annotation { "Feature Type Name" : "Feature", "Feature Type Description" : "" }
export const myFeature = defineFeature(function(context is Context, id is Id, definition is map)
    precondition{}
    {
        {
            var Q0;
            Q0=qCreatedBy(makeId("Front.planeOp"),FACE);
            var sketch = newSketch(context, id + "F0", { "sketchPlane" : qUnion([Q0])});
            skLineSegment(sketch, "E0.bottom", {"start": v(-44.68, 30.46) * mm, "end": v(44.68, 30.46) * mm});
            skLineSegment(sketch, "E0.top", {"start": v(-44.68, -30.46) * mm, "end": v(44.68, -30.46) * mm});
            skLineSegment(sketch, "E0.left", {"start": v(-44.68, 30.46) * mm, "end": v(-44.68, -30.46) * mm});
            skLineSegment(sketch, "E0.right", {"start": v(44.68, 30.46) * mm, "end": v(44.68, -30.46) * mm});
            skPoint(sketch, "E0.middle", {"position": v(0, 0) * mm});
            skSolve(sketch);
        }
        {
            var Q0;
            Q0=makeQuery(id+"F0.imprint","IMPRINT",FACE,{"disambiguationData":[TD([[makeQuery(id+"F0.imprint","IMPRINT",EDGE,{"derivedFrom":sQuery(id+"F0.wireOp",EDGE,"E0.bottom")}),-1.0]])]});
            extrude(context, id + "F1", {"entities" : qUnion([Q0]), "endBound" : BoundingType.SYMMETRIC, "depth" : 99.2 * mm});
        }
        {
            var Q0;
            Q0=makeQuery(id+"F1.opExtrude","SWEPT_FACE",FACE,{"disambiguationData":[OSD([sQuery(id+"F0.wireOp",EDGE,"E0.bottom")])]});
            shell(context, id + "F2", {"entities" : qUnion([Q0]), "thickness" : 2.5 * mm});
        }
        {
            var Q0;
            Q0=makeQuery(id+"F1.opExtrude","CAP_FACE",FACE,{"disambiguationData":[OSD([sQuery(id+"F0.wireOp",EDGE,"E0.bottom"),sQuery(id+"F0.wireOp",EDGE,"E0.top"),sQuery(id+"F0.wireOp",EDGE,"E0.left"),sQuery(id+"F0.wireOp",EDGE,"E0.right")])],"isStart":false});
            var sketch = newSketch(context, id + "F3", { "sketchPlane" : qUnion([Q0])});
            skLineSegment(sketch, "E1.bottom", {"start": v(-44.68, 30.46) * mm, "end": v(-36.59, 30.46) * mm});
            skLineSegment(sketch, "E1.top", {"start": v(-44.68, -30.46) * mm, "end": v(-36.59, -30.46) * mm});
            skLineSegment(sketch, "E1.left", {"start": v(-44.68, 30.46) * mm, "end": v(-44.68, -30.46) * mm});
            skLineSegment(sketch, "E1.right", {"start": v(-36.59, 30.46) * mm, "end": v(-36.59, -30.46) * mm});
            skLineSegment(sketch, "E2.bottom", {"start": v(44.68, 30.46) * mm, "end": v(36.58, 30.46) * mm});
            skLineSegment(sketch, "E2.top", {"start": v(44.68, -30.46) * mm, "end": v(36.58, -30.46) * mm});
            skLineSegment(sketch, "E2.left", {"start": v(44.68, 30.46) * mm, "end": v(44.68, -30.46) * mm});
            skLineSegment(sketch, "E2.right", {"start": v(36.58, 30.46) * mm, "end": v(36.58, -30.46) * mm});
            skSolve(sketch);
        }
        {
            var Q0;
            Q0=makeQuery(id+"F3.imprint","IMPRINT",FACE,{"disambiguationData":[TD([[makeQuery(id+"F3.imprint","IMPRINT",EDGE,{"derivedFrom":sQuery(id+"F3.wireOp",EDGE,"E1.bottom")}),-1.0]])]});
            var Q1;
            Q1=makeQuery(id+"F3.imprint","IMPRINT",FACE,{"disambiguationData":[TD([[makeQuery(id+"F3.imprint","IMPRINT",EDGE,{"derivedFrom":sQuery(id+"F3.wireOp",EDGE,"E2.bottom")}),-1.0]])]});
            extrude(context, id + "F4", {"entities" : qUnion([Q0, Q1]), "operationType" : NewBodyOperationType.ADD, "depth" : 2.8 * mm});
        }
        {
            var Q0;
            Q0=makeQuery(id+"F4.opExtrude","CAP_FACE",FACE,{"disambiguationData":[OSD([sQuery(id+"F3.wireOp",EDGE,"E1.bottom"),sQuery(id+"F3.wireOp",EDGE,"E1.top"),sQuery(id+"F3.wireOp",EDGE,"E1.left"),sQuery(id+"F3.wireOp",EDGE,"E1.right")])],"isStart":false});
            var Q1;
            Q1=makeQuery(id+"F4.opExtrude","CAP_FACE",FACE,{"disambiguationData":[OSD([sQuery(id+"F3.wireOp",EDGE,"E2.bottom"),sQuery(id+"F3.wireOp",EDGE,"E2.top"),sQuery(id+"F3.wireOp",EDGE,"E2.left"),sQuery(id+"F3.wireOp",EDGE,"E2.right")])],"isStart":false});
            var Q2;
            Q2=makeQuery(id+"F1.opExtrude","CAP_FACE",FACE,{"disambiguationData":[OSD([sQuery(id+"F0.wireOp",EDGE,"E0.bottom"),sQuery(id+"F0.wireOp",EDGE,"E0.top"),sQuery(id+"F0.wireOp",EDGE,"E0.left"),sQuery(id+"F0.wireOp",EDGE,"E0.right")])],"isStart":true});
            shell(context, id + "F5", {"entities" : qUnion([Q0, Q1, Q2]), "thickness" : 2.5 * mm});
        }
        {
            var Q0;
            Q0=makeQuery(id+"F4.boolean.opBoolean","MERGE",FACE,{"derivedFrom":[makeQuery(id+"F1.opExtrude","SWEPT_FACE",FACE,{"disambiguationData":[OSD([sQuery(id+"F0.wireOp",EDGE,"E0.right")])]}),makeQuery(id+"F4.opExtrude","SWEPT_FACE",FACE,{"disambiguationData":[OSD([sQuery(id+"F3.wireOp",EDGE,"E2.left")])]})]});
            var sketch = newSketch(context, id + "F6", { "sketchPlane" : qUnion([Q0])});
            skLineSegment(sketch, "E3.bottom", {"start": v(-52.4, 30.46) * mm, "end": v(-44.7, 30.46) * mm});
            skLineSegment(sketch, "E3.top", {"start": v(-52.4, -30.46) * mm, "end": v(-44.7, -30.46) * mm});
            skLineSegment(sketch, "E3.left", {"start": v(-52.4, 30.46) * mm, "end": v(-52.4, -30.46) * mm});
            skLineSegment(sketch, "E3.right", {"start": v(-44.7, 30.46) * mm, "end": v(-44.7, -30.46) * mm});
            skSolve(sketch);
        }
        {
            var Q0;
            Q0=makeQuery(id+"F6.imprint","IMPRINT",FACE,{"disambiguationData":[TD([[makeQuery(id+"F6.imprint","IMPRINT",EDGE,{"derivedFrom":sQuery(id+"F6.wireOp",EDGE,"E3.bottom")}),-1.0]])]});
            extrude(context, id + "F7", {"entities" : qUnion([Q0]), "operationType" : NewBodyOperationType.ADD, "depth" : 1 * mm});
        }
        {
            var Q0;
            Q0=makeQuery(id+"F7.opExtrude","CAP_FACE",FACE,{"disambiguationData":[OSD([sQuery(id+"F6.wireOp",EDGE,"E3.bottom"),sQuery(id+"F6.wireOp",EDGE,"E3.top"),sQuery(id+"F6.wireOp",EDGE,"E3.left"),sQuery(id+"F6.wireOp",EDGE,"E3.right")])],"isStart":false});
            var Q1;
            Q1=makeQuery(id+"F5.opShell","OFFSET_FACE",FACE,{"disambiguationData":[OSD([sQuery(id+"F0.wireOp",EDGE,"E0.left"),sQuery(id+"F3.wireOp",EDGE,"E1.left")])]});
            shell(context, id + "F8", {"entities" : qUnion([Q0, Q1]), "thickness" : 2.5 * mm});
        }
        {
            var Q0;
            Q0=makeQuery(id+"F4.boolean.opBoolean","MERGE",FACE,{"derivedFrom":[makeQuery(id+"F1.opExtrude","SWEPT_FACE",FACE,{"disambiguationData":[OSD([sQuery(id+"F0.wireOp",EDGE,"E0.left")])]}),makeQuery(id+"F4.opExtrude","SWEPT_FACE",FACE,{"disambiguationData":[OSD([sQuery(id+"F3.wireOp",EDGE,"E1.left")])]})]});
            var sketch = newSketch(context, id + "F9", { "sketchPlane" : qUnion([Q0])});
            skLineSegment(sketch, "E4.bottom", {"start": v(-49.6, 30.46) * mm, "end": v(-40.98, 30.46) * mm});
            skLineSegment(sketch, "E4.top", {"start": v(-49.6, -30.46) * mm, "end": v(-40.98, -30.46) * mm});
            skLineSegment(sketch, "E4.left", {"start": v(-49.6, 30.46) * mm, "end": v(-49.6, -30.46) * mm});
            skLineSegment(sketch, "E4.right", {"start": v(-40.98, 30.46) * mm, "end": v(-40.98, -30.46) * mm});
            skLineSegment(sketch, "E5.bottom", {"start": v(52.4, 30.46) * mm, "end": v(44.29, 30.46) * mm});
            skLineSegment(sketch, "E5.top", {"start": v(52.4, -30.46) * mm, "end": v(44.29, -30.46) * mm});
            skLineSegment(sketch, "E5.left", {"start": v(52.4, 30.46) * mm, "end": v(52.4, -30.46) * mm});
            skLineSegment(sketch, "E5.right", {"start": v(44.29, 30.46) * mm, "end": v(44.29, -30.46) * mm});
            skSolve(sketch);
        }
        {
            var Q0;
            Q0=makeQuery(id+"F9.imprint","IMPRINT",FACE,{"disambiguationData":[TD([[makeQuery(id+"F9.imprint","IMPRINT",EDGE,{"derivedFrom":sQuery(id+"F9.wireOp",EDGE,"E4.bottom")}),1.0]])]});
            var Q1;
            Q1=makeQuery(id+"F9.imprint","IMPRINT",FACE,{"disambiguationData":[TD([[makeQuery(id+"F9.imprint","IMPRINT",EDGE,{"derivedFrom":sQuery(id+"F9.wireOp",EDGE,"E5.bottom")}),1.0]])]});
            extrude(context, id + "F10", {"entities" : qUnion([Q0, Q1]), "operationType" : NewBodyOperationType.ADD, "depth" : 1.9 * mm});
        }
        {
            var Q0;
            Q0=makeQuery(id+"F10.opExtrude","CAP_FACE",FACE,{"disambiguationData":[OSD([sQuery(id+"F9.wireOp",EDGE,"E4.bottom"),sQuery(id+"F9.wireOp",EDGE,"E4.top"),sQuery(id+"F9.wireOp",EDGE,"E4.left"),sQuery(id+"F9.wireOp",EDGE,"E4.right")])],"isStart":false});
            var Q1;
            Q1=makeQuery(id+"F10.opExtrude","CAP_FACE",FACE,{"disambiguationData":[OSD([sQuery(id+"F9.wireOp",EDGE,"E5.bottom"),sQuery(id+"F9.wireOp",EDGE,"E5.top"),sQuery(id+"F9.wireOp",EDGE,"E5.left"),sQuery(id+"F9.wireOp",EDGE,"E5.right")])],"isStart":false});
            shell(context, id + "F11", {"entities" : qUnion([Q0, Q1]), "thickness" : 2.5 * mm});
        }
        {
            var Q0;
            Q0=makeQuery(id+"F10.boolean.opBoolean","MERGE",FACE,{"derivedFrom":[makeQuery(id+"F1.opExtrude","CAP_FACE",FACE,{"disambiguationData":[OSD([sQuery(id+"F0.wireOp",EDGE,"E0.bottom"),sQuery(id+"F0.wireOp",EDGE,"E0.top"),sQuery(id+"F0.wireOp",EDGE,"E0.left"),sQuery(id+"F0.wireOp",EDGE,"E0.right")])],"isStart":true}),makeQuery(id+"F10.opExtrude","SWEPT_FACE",FACE,{"disambiguationData":[OSD([sQuery(id+"F9.wireOp",EDGE,"E4.left")])]})]});
            var sketch = newSketch(context, id + "F12", { "sketchPlane" : qUnion([Q0])});
            skSolve(sketch);
        }
        {
            var Q0;
            Q0=makeQuery(id+"F4.boolean.opBoolean","MERGE",FACE,{"derivedFrom":[makeQuery(id+"F1.opExtrude","SWEPT_FACE",FACE,{"disambiguationData":[OSD([sQuery(id+"F0.wireOp",EDGE,"E0.right")])]}),makeQuery(id+"F4.opExtrude","SWEPT_FACE",FACE,{"disambiguationData":[OSD([sQuery(id+"F3.wireOp",EDGE,"E2.left")])]})]});
            var sketch = newSketch(context, id + "F13", { "sketchPlane" : qUnion([Q0])});
            skLineSegment(sketch, "E6.bottom", {"start": v(49.6, 30.46) * mm, "end": v(39.53, 30.46) * mm});
            skLineSegment(sketch, "E6.top", {"start": v(49.6, -30.46) * mm, "end": v(39.53, -30.46) * mm});
            skLineSegment(sketch, "E6.left", {"start": v(49.6, 30.46) * mm, "end": v(49.6, -30.46) * mm});
            skLineSegment(sketch, "E6.right", {"start": v(39.53, 30.46) * mm, "end": v(39.53, -30.46) * mm});
            skSolve(sketch);
        }
        {
            var Q0;
            Q0=makeQuery(id+"F13.imprint","IMPRINT",FACE,{"disambiguationData":[TD([[makeQuery(id+"F13.imprint","IMPRINT",EDGE,{"derivedFrom":sQuery(id+"F13.wireOp",EDGE,"E6.bottom")}),-1.0]])]});
            extrude(context, id + "F14", {"entities" : qUnion([Q0]), "operationType" : NewBodyOperationType.ADD, "depth" : 2.5 * mm});
        }
        {
            var Q0;
            Q0=makeQuery(id+"F14.opExtrude","CAP_FACE",FACE,{"disambiguationData":[OSD([sQuery(id+"F13.wireOp",EDGE,"E6.bottom"),sQuery(id+"F13.wireOp",EDGE,"E6.top"),sQuery(id+"F13.wireOp",EDGE,"E6.left"),sQuery(id+"F13.wireOp",EDGE,"E6.right")])],"isStart":false});
            shell(context, id + "F15", {"entities" : qUnion([Q0]), "thickness" : 2.5 * mm});
        }
        {
            var Q0;
            Q0=makeQuery(id+"F14.boolean.opBoolean","MERGE",FACE,{"derivedFrom":[makeQuery(id+"F10.boolean.opBoolean","MERGE",FACE,{"derivedFrom":[makeQuery(id+"F1.opExtrude","CAP_FACE",FACE,{"disambiguationData":[OSD([sQuery(id+"F0.wireOp",EDGE,"E0.bottom"),sQuery(id+"F0.wireOp",EDGE,"E0.top"),sQuery(id+"F0.wireOp",EDGE,"E0.left"),sQuery(id+"F0.wireOp",EDGE,"E0.right")])],"isStart":true}),makeQuery(id+"F10.opExtrude","SWEPT_FACE",FACE,{"disambiguationData":[OSD([sQuery(id+"F9.wireOp",EDGE,"E4.left")])]})]}),makeQuery(id+"F14.opExtrude","SWEPT_FACE",FACE,{"disambiguationData":[OSD([sQuery(id+"F13.wireOp",EDGE,"E6.left")])]})]});
            var sketch = newSketch(context, id + "F16", { "sketchPlane" : qUnion([Q0])});
            skLineSegment(sketch, "E7.bottom", {"start": v(-47.18, 30.46) * mm, "end": v(-37.77, 30.46) * mm});
            skLineSegment(sketch, "E7.top", {"start": v(-47.18, -30.46) * mm, "end": v(-37.77, -30.46) * mm});
            skLineSegment(sketch, "E7.left", {"start": v(-47.18, 30.46) * mm, "end": v(-47.18, -30.46) * mm});
            skLineSegment(sketch, "E7.right", {"start": v(-37.77, 30.46) * mm, "end": v(-37.77, -30.46) * mm});
            skLineSegment(sketch, "E8.bottom", {"start": v(46.58, 30.46) * mm, "end": v(36.94, 30.46) * mm});
            skLineSegment(sketch, "E8.top", {"start": v(46.58, -30.46) * mm, "end": v(36.94, -30.46) * mm});
            skLineSegment(sketch, "E8.left", {"start": v(46.58, 30.46) * mm, "end": v(46.58, -30.46) * mm});
            skLineSegment(sketch, "E8.right", {"start": v(36.94, 30.46) * mm, "end": v(36.94, -30.46) * mm});
            skSolve(sketch);
        }
        {
            var Q0;
            Q0 = qSketchRegion(id + "F16", true);
            extrude(context, id + "F17", {"entities" : qUnion([Q0]), "operationType" : NewBodyOperationType.ADD, "depth" : 1.4 * mm});
        }
        {
            var Q0;
            Q0=makeQuery(id+"F17.opExtrude","CAP_FACE",FACE,{"disambiguationData":[OSD([sQuery(id+"F16.wireOp",EDGE,"E7.bottom"),sQuery(id+"F16.wireOp",EDGE,"E7.top"),sQuery(id+"F16.wireOp",EDGE,"E7.left"),sQuery(id+"F16.wireOp",EDGE,"E7.right")])],"isStart":false});
            var Q1;
            Q1=makeQuery(id+"F17.opExtrude","CAP_FACE",FACE,{"disambiguationData":[OSD([sQuery(id+"F16.wireOp",EDGE,"E8.bottom"),sQuery(id+"F16.wireOp",EDGE,"E8.top"),sQuery(id+"F16.wireOp",EDGE,"E8.left"),sQuery(id+"F16.wireOp",EDGE,"E8.right")])],"isStart":false});
            shell(context, id + "F18", {"entities" : qUnion([Q0, Q1]), "thickness" : 2.5 * mm});
        }
        {
            var Q0;
            Q0=makeQuery(id+"F10.opExtrude","CAP_EDGE",EDGE,{"disambiguationData":[OSD([sQuery(id+"F9.wireOp",EDGE,"E5.left")])],"isStart":false});
            var Q1;
            Q1=makeQuery(id+"F7.opExtrude","CAP_EDGE",EDGE,{"disambiguationData":[OSD([sQuery(id+"F6.wireOp",EDGE,"E3.left")])],"isStart":false});
            var Q2;
            Q2=makeQuery(id+"F17.opExtrude","CAP_EDGE",EDGE,{"disambiguationData":[OSD([sQuery(id+"F16.wireOp",EDGE,"E7.left")])],"isStart":false});
            var Q3;
            Q3=makeQuery(id+"F17.opExtrude","CAP_EDGE",EDGE,{"disambiguationData":[OSD([sQuery(id+"F16.wireOp",EDGE,"E8.left")])],"isStart":false});
            fillet(context, id + "F19", {"entities" : qUnion([Q0, Q1, Q2, Q3]), "radius" : 5 * mm, "tangentPropagation" : true, "allowEdgeOverflow" : false});
        }
        {
            var Q0;
            Q0=makeQuery(id+"F12.imprint","IMPRINT",FACE,{"disambiguationData":[TD([[makeQuery(id+"F12.imprint","IMPRINT",EDGE,{"derivedFrom":makeQuery(id+"F1.opExtrude","CAP_EDGE",EDGE,{"disambiguationData":[OSD([sQuery(id+"F0.wireOp",EDGE,"E0.right")])],"isStart":true})}),1.0]])]});
            var sketch = newSketch(context, id + "F20", { "sketchPlane" : qUnion([Q0])});
            skText(sketch, "E9", { "text": "Yellow Jacket\n     Football", "fontName": "DroidSansMono.ttf"});
            const initialGuessF20  = {"E9": [-0.03725, 0, 1, 0, 0.00528]};
            skSetInitialGuess(sketch, initialGuessF20);
            skSolve(sketch);
        }
        {
            var Q0;
            Q0 = qConstructionFilter(qBodyType(qCreatedBy(id + "F20" ,EDGE), BodyType.WIRE), ConstructionObject.NO);
            extrude(context, id + "F21", {"bodyType" : ToolBodyType.SURFACE, "surfaceEntities" : qUnion([Q0]), "depth" : 1.6 * mm});
        }
        {
            var Q0;
            Q0=makeQuery(id+"F1.opExtrude","CAP_FACE",FACE,{"disambiguationData":[OSD([sQuery(id+"F0.wireOp",EDGE,"E0.bottom"),sQuery(id+"F0.wireOp",EDGE,"E0.top"),sQuery(id+"F0.wireOp",EDGE,"E0.left"),sQuery(id+"F0.wireOp",EDGE,"E0.right")])],"isStart":false});
            var sketch = newSketch(context, id + "F22", { "sketchPlane" : qUnion([Q0])});
            skText(sketch, "E10", { "text": "Yellow Jacket \n  Football", "fontName": "DroidSansMono.ttf"});
            skPoint(sketch, "E10.secondSnap0", {"position": v(-36.59, 0) * mm});
            const initialGuessF22  = {"E10": [-0.03158, 0, 1, 0, 0.0052]};
            skSetInitialGuess(sketch, initialGuessF22);
            skSolve(sketch);
        }
        {
            var Q0;
            Q0 = qSketchRegion(id + "F22", true);
            extrude(context, id + "F23", {"entities" : qUnion([Q0]), "operationType" : NewBodyOperationType.ADD, "depth" : 0.6 * mm});
        }
        {
            var Q0;
            Q0=makeQuery(id+"F4.boolean.opBoolean","MERGE",FACE,{"derivedFrom":[makeQuery(id+"F1.opExtrude","SWEPT_FACE",FACE,{"disambiguationData":[OSD([sQuery(id+"F0.wireOp",EDGE,"E0.right")])]}),makeQuery(id+"F4.opExtrude","SWEPT_FACE",FACE,{"disambiguationData":[OSD([sQuery(id+"F3.wireOp",EDGE,"E2.left")])]})]});
            var sketch = newSketch(context, id + "F24", { "sketchPlane" : qUnion([Q0])});
            skText(sketch, "E11", { "text": "STATE CHAMPS", "fontName": "DroidSansMono.ttf"});
            skPoint(sketch, "E11.firstSnap0", {"position": v(-44.7, 0) * mm});
            const initialGuessF24  = {"E11": [-0.0443, 0, 1, 0, 0.0082]};
            skSetInitialGuess(sketch, initialGuessF24);
            skSolve(sketch);
        }
        {
            var Q0;
            Q0 = qSketchRegion(id + "F24", true);
            extrude(context, id + "F25", {"entities" : qUnion([Q0]), "operationType" : NewBodyOperationType.ADD, "depth" : 1 * mm});
        }
        {
            var Q0;
            Q0=makeQuery(id+"F4.boolean.opBoolean","MERGE",FACE,{"derivedFrom":[makeQuery(id+"F1.opExtrude","SWEPT_FACE",FACE,{"disambiguationData":[OSD([sQuery(id+"F0.wireOp",EDGE,"E0.left")])]}),makeQuery(id+"F4.opExtrude","SWEPT_FACE",FACE,{"disambiguationData":[OSD([sQuery(id+"F3.wireOp",EDGE,"E1.left")])]})]});
            var sketch = newSketch(context, id + "F26", { "sketchPlane" : qUnion([Q0])});
            skText(sketch, "E12", { "text": "STATE CHAMPS\n", "fontName": "OpenSans-Regular.ttf"});
            const initialGuessF26  = {"E12": [-0.03823, 0, 1, 0, 0.008]};
            skSetInitialGuess(sketch, initialGuessF26);
            skSolve(sketch);
        }
        {
            var Q0;
            Q0 = qSketchRegion(id + "F26", true);
            extrude(context, id + "F27", {"entities" : qUnion([Q0]), "operationType" : NewBodyOperationType.ADD, "depth" : 1 * mm});
        }
    });